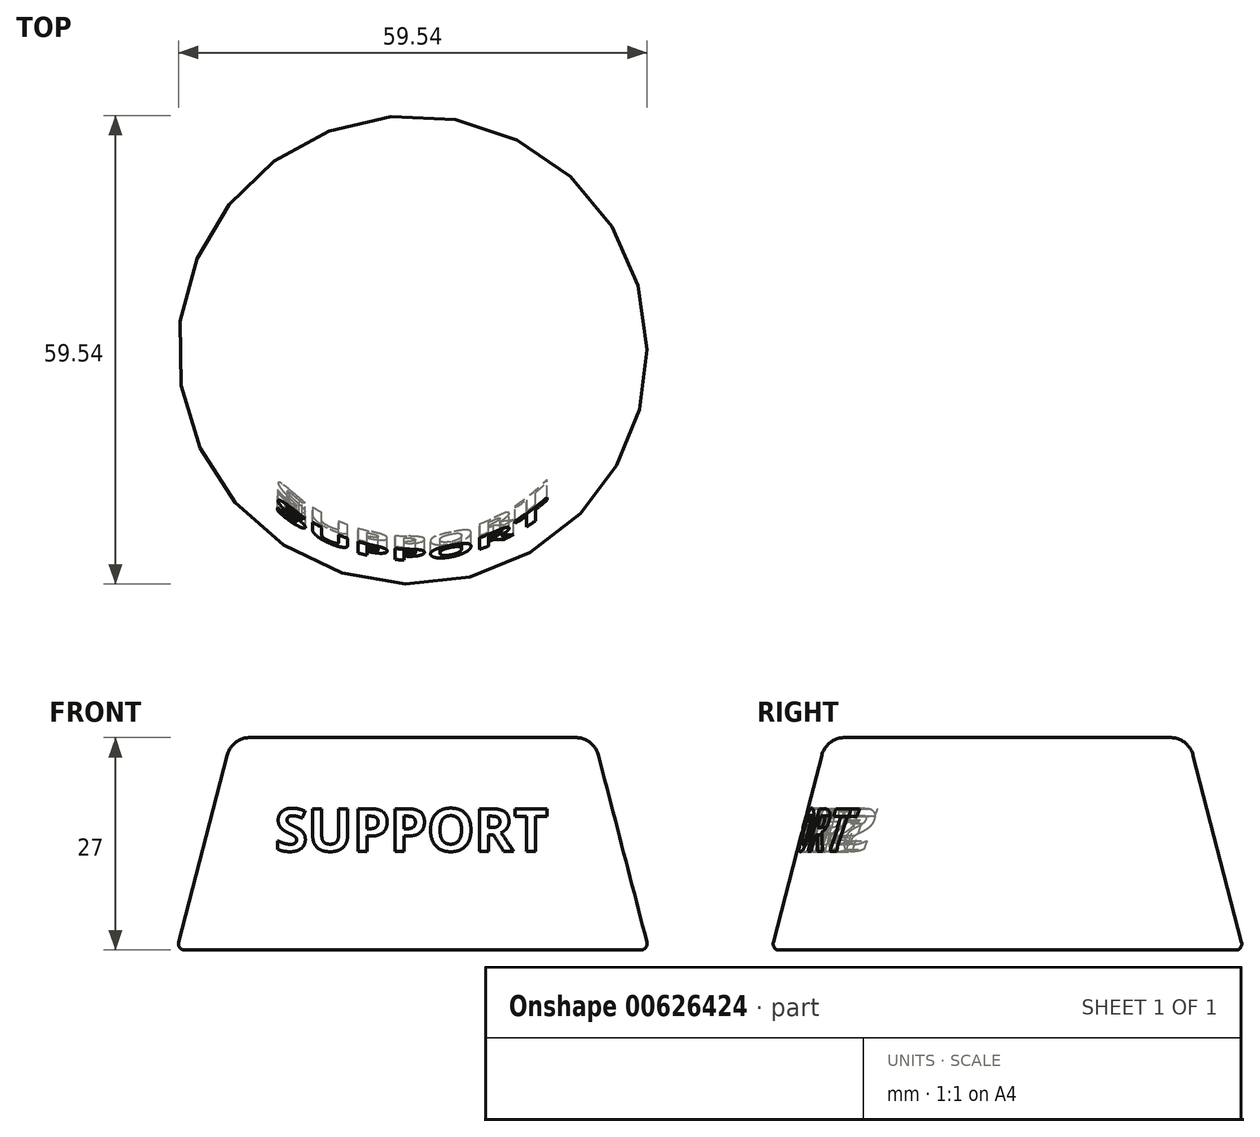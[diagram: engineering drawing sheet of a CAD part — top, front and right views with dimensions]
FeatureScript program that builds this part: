
annotation { "Feature Type Name" : "Feature", "Feature Type Description" : "" }
export const myFeature = defineFeature(function(context is Context, id is Id, definition is map)
    precondition{}
    {
        {
            var Q0;
            Q0=qCreatedBy(makeId("Front.planeOp"),FACE);
            var sketch = newSketch(context, id + "F0", { "sketchPlane" : qUnion([Q0])});
            skLineSegment(sketch, "E0", {"start": v(0, 7.01) * mm, "end": v(-23, 7.01) * mm});
            skLineSegment(sketch, "E1", {"start": v(-23, 7.01) * mm, "end": v(-30, -19.99) * mm});
            skLineSegment(sketch, "E2", {"start": v(-30, -19.99) * mm, "end": v(0, -19.99) * mm});
            skLineSegment(sketch, "E3", {"start": v(0, -19.99) * mm, "end": v(0, 7.01) * mm});
            skSolve(sketch);
        }
        {
            var Q0;
            Q0=makeQuery(id+"F0.imprint","IMPRINT",FACE,{"disambiguationData":[TD([[makeQuery(id+"F0.imprint","IMPRINT",EDGE,{"derivedFrom":sQuery(id+"F0.wireOp",EDGE,"E0")}),1.0]])]});
            var Q1;
            Q1=sQuery(id+"F0.wireOp",EDGE,"E3");
            revolve(context, id + "F1", {"entities" : qUnion([Q0]), "axis" : qUnion([Q1]), "revolveType" : RevolveType.FULL});
        }
        {
            var Q0;
            Q0=qCreatedBy(makeId("Right.planeOp"),FACE);
            var sketch = newSketch(context, id + "F2", { "sketchPlane" : qUnion([Q0])});
            skLineSegment(sketch, "E4", {"start": v(-41.63, 34.27) * mm, "end": v(-25.16, 13.83) * mm});
            skLineSegment(sketch, "E5", {"start": v(-25.16, 13.83) * mm, "end": v(-27.3, -6.06) * mm});
            skLineSegment(sketch, "E6", {"start": v(-27.3, -6.06) * mm, "end": v(-54.66, -28.12) * mm});
            skLineSegment(sketch, "E7", {"start": v(-54.66, -28.12) * mm, "end": v(-41.63, 34.27) * mm});
            skSolve(sketch);
        }
        {
            var Q0;
            Q0=qCreatedBy(makeId("Right.planeOp"),FACE);
            var sketch = newSketch(context, id + "F3", { "sketchPlane" : qUnion([Q0])});
            skLineSegment(sketch, "E8", {"start": v(-26.95, 33.93) * mm, "end": v(-76, 38.48) * mm});
            skLineSegment(sketch, "E9", {"start": v(-76, 38.48) * mm, "end": v(-33.97, -50.8) * mm});
            skLineSegment(sketch, "E10", {"start": v(-33.97, -50.8) * mm, "end": v(-26.95, 33.93) * mm});
            skSolve(sketch);
        }
        {
            var Q0;
            Q0=qCreatedBy(makeId("Front.planeOp"),FACE);
            var sketch = newSketch(context, id + "F4", { "sketchPlane" : qUnion([Q0])});
            skText(sketch, "E11", { "text": "SUPPORT", "fontName": "OpenSans-Bold.ttf"});
            skLineSegment(sketch, "E12.0", {"start": v(23, 7.01) * mm, "end": v(-23, 7.01) * mm});
            const initialGuessF4  = {"E11": [-0.0175, -0.00742, 1, 0, 0.00543]};
            skSetInitialGuess(sketch, initialGuessF4);
            skSolve(sketch);
        }
        {
            var Q0;
            Q0 = qSketchRegion(id + "F4", true);
            extrude(context, id + "F5", {"entities" : qUnion([Q0]), "operationType" : NewBodyOperationType.REMOVE, "endBound" : BoundingType.THROUGH_ALL, "depth" : 25 * mm, "offsetDistance" : 25 * mm});
        }
        {
            var Q0;
            Q0=qCreatedBy(makeId("Front.planeOp"),FACE);
            var sketch = newSketch(context, id + "F6", { "sketchPlane" : qUnion([Q0])});
            skLineSegment(sketch, "E13", {"start": v(0, 7.01) * mm, "end": v(-21.35, 7.01) * mm});
            skLineSegment(sketch, "E14", {"start": v(-21.35, 7.01) * mm, "end": v(-28.35, -19.99) * mm});
            skLineSegment(sketch, "E15", {"start": v(-28.35, -19.99) * mm, "end": v(0, -19.99) * mm});
            skLineSegment(sketch, "E16", {"start": v(0, -19.99) * mm, "end": v(0, 7.01) * mm});
            skLineSegment(sketch, "E17", {"start": v(-21.35, 7.01) * mm, "end": v(0, 7.01) * mm});
            skLineSegment(sketch, "E18", {"start": v(0, -19.99) * mm, "end": v(-28.35, -19.99) * mm});
            skLineSegment(sketch, "E19", {"start": v(-30.63, -22.42) * mm, "end": v(-22.3, 9.75) * mm});
            skSolve(sketch);
        }
        {
            var Q0;
            Q0 = qSketchRegion(id + "F6", true);
            var Q1;
            Q1=sQuery(id+"F6.wireOp",EDGE,"E16");
            revolve(context, id + "F7", {"operationType" : NewBodyOperationType.ADD, "entities" : qUnion([Q0]), "axis" : qUnion([Q1]), "revolveType" : RevolveType.FULL});
        }
        {
            var Q0;
            Q0=qCreatedBy(makeId("Front.planeOp"),FACE);
            var sketch = newSketch(context, id + "F8", { "sketchPlane" : qUnion([Q0])});
            skLineSegment(sketch, "E20", {"start": v(-23.3, 9.75) * mm, "end": v(-31.63, -22.42) * mm});
            skSolve(sketch);
        }
        {
            var Q0;
            Q0=makeQuery(id+"F1.opRevolve","SWEPT_EDGE",EDGE,{"disambiguationData":[OSD([sQuery(id+"F0.wireOp",EDGE,"E0"),sQuery(id+"F0.wireOp",EDGE,"E1")])]});
            fillet(context, id + "F9", {"entities" : qUnion([Q0]), "radius" : 3 * mm, "tangentPropagation" : true, "allowEdgeOverflow" : false});
        }
        {
            var Q0;
            Q0=makeQuery(id+"F1.opRevolve","SWEPT_EDGE",EDGE,{"disambiguationData":[OSD([sQuery(id+"F0.wireOp",EDGE,"E1"),sQuery(id+"F0.wireOp",EDGE,"E2")])]});
            fillet(context, id + "F10", {"entities" : qUnion([Q0]), "radius" : 0.8 * mm, "tangentPropagation" : true, "allowEdgeOverflow" : false});
        }
    });
